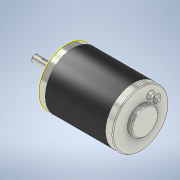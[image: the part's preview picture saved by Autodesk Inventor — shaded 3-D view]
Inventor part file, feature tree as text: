
AUTODESK INVENTOR PART (.ipt)
format: ipt  version: 2020 (Build 240168000, 168)  size: 192,000 bytes
history: native  units: in
note: dims shown in document units (in); Inventor stores cm internally (conversion verified against a paired STEP export)
features: sketch x1, chamfer x1
ambient origin geometry x8: Origin, YZ Plane, XZ Plane, XY Plane, X Axis, Y Axis, Z Axis, Center Point
bodies: Solid1 (feature_tree)
feature tree (2):
  sketch  "Sketch1"
  chamfer  "Chamfer3"  [1 undecoded]
note: 1 required parameter value undecoded (feature->parameter linkage not recoverable at this tier; creation-order binding heuristic only, values carry confidence <= 0.55)
